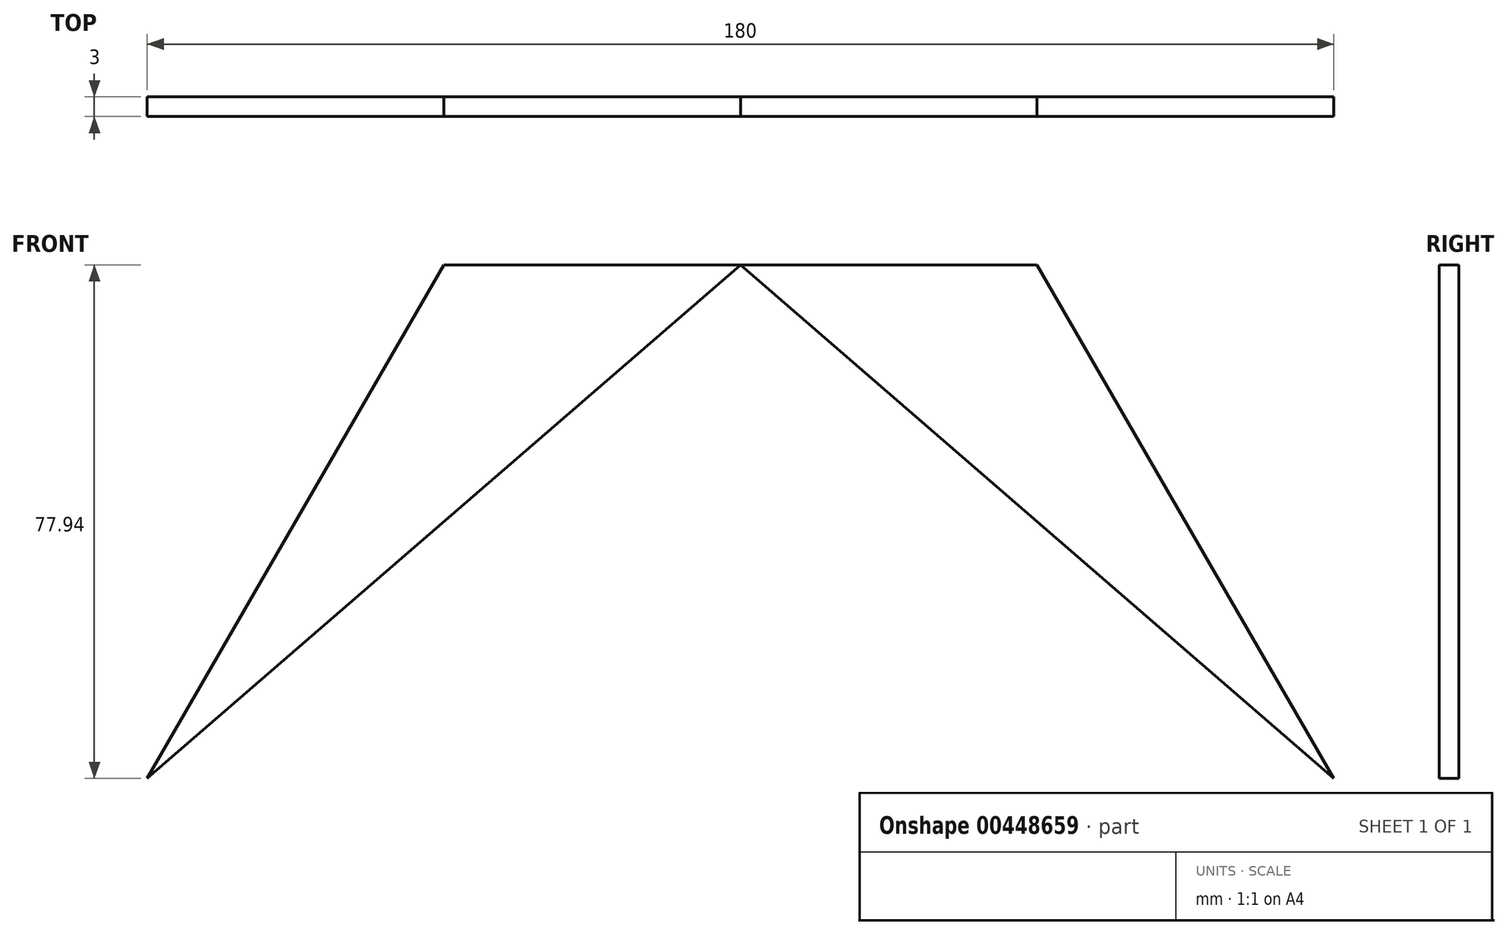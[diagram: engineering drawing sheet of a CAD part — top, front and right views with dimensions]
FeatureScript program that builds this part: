
annotation { "Feature Type Name" : "Feature", "Feature Type Description" : "" }
export const myFeature = defineFeature(function(context is Context, id is Id, definition is map)
    precondition{}
    {
        {
            var Q0;
            Q0=qCreatedBy(makeId("Front.planeOp"),FACE);
            var sketch = newSketch(context, id + "F0", { "sketchPlane" : qUnion([Q0])});
            skLineSegment(sketch, "E0.0", {"start": v(45, 77.94) * mm, "end": v(90, 0) * mm});
            skLineSegment(sketch, "E0.4", {"start": v(-90, 0) * mm, "end": v(-45, 77.94) * mm});
            skLineSegment(sketch, "E0.5", {"start": v(-45, 77.94) * mm, "end": v(45, 77.94) * mm});
            skLineSegment(sketch, "E1", {"start": v(0, 77.94) * mm, "end": v(-90, 0) * mm});
            skLineSegment(sketch, "E2", {"start": v(0, 77.94) * mm, "end": v(90, 0) * mm});
            skLineSegment(sketch, "E3", {"start": v(-90, 0) * mm, "end": v(90, 0) * mm, "construction": true});
            skLineSegment(sketch, "E4", {"start": v(0, 77.94) * mm, "end": v(0, 0) * mm, "construction": true});
            skSolve(sketch);
        }
        {
            var Q0;
            Q0 = qSketchRegion(id + "F0", true);
            extrude(context, id + "F1", {"entities" : qUnion([Q0]), "depth" : 3 * mm});
        }
    });
